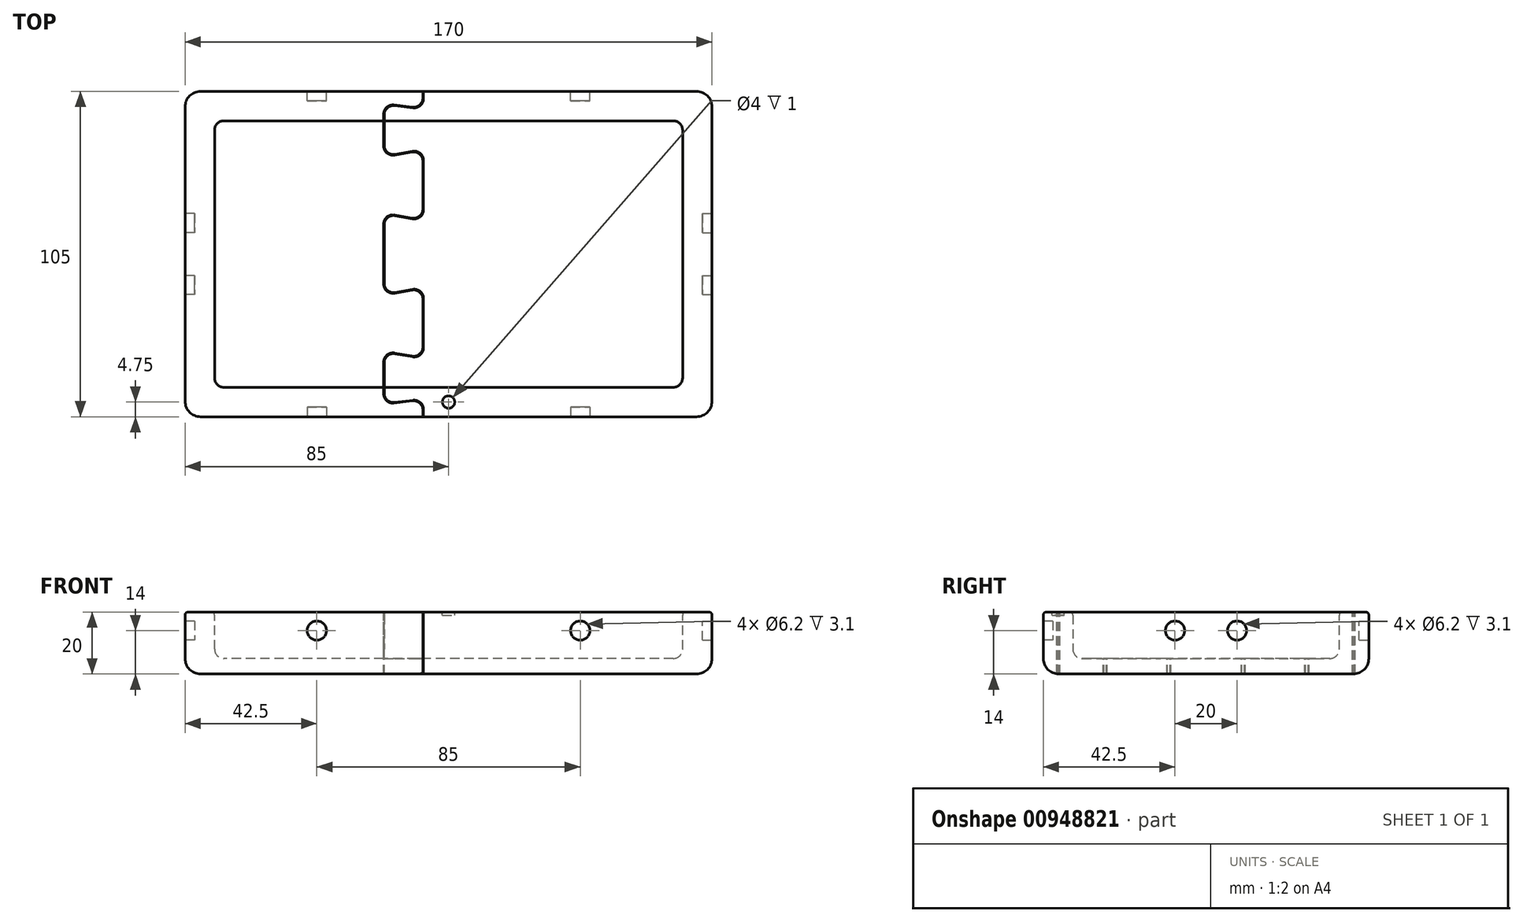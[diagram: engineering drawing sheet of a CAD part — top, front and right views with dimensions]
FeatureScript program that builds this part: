
annotation { "Feature Type Name" : "Feature", "Feature Type Description" : "" }
export const myFeature = defineFeature(function(context is Context, id is Id, definition is map)
    precondition{}
    {
        {
            var Q0;
            Q0=qCreatedBy(makeId("Top.planeOp"),FACE);
            var sketch = newSketch(context, id + "F0", { "sketchPlane" : qUnion([Q0])});
            skLineSegment(sketch, "E0.bottom", {"start": v(-85, 52.5) * mm, "end": v(85, 52.5) * mm});
            skLineSegment(sketch, "E0.top", {"start": v(-85, -52.5) * mm, "end": v(85, -52.5) * mm});
            skLineSegment(sketch, "E0.left", {"start": v(-85, 52.5) * mm, "end": v(-85, -52.5) * mm});
            skLineSegment(sketch, "E0.right", {"start": v(85, 52.5) * mm, "end": v(85, -52.5) * mm});
            skLineSegment(sketch, "E1.bottom", {"start": v(-72.5, 43) * mm, "end": v(72.5, 43) * mm});
            skLineSegment(sketch, "E1.top", {"start": v(-72.5, -43) * mm, "end": v(72.5, -43) * mm});
            skLineSegment(sketch, "E1.left", {"start": v(-75.5, 40) * mm, "end": v(-75.5, -40) * mm});
            skLineSegment(sketch, "E1.right", {"start": v(75.5, 40) * mm, "end": v(75.5, -40) * mm});
            skLineSegment(sketch, "E2.direction1", {"start": v(-75.5, -43) * mm, "end": v(15.26, -43) * mm, "construction": true});
            skPoint(sketch, "E3.visualSharp", {"position": v(-75.5, 43) * mm});
            skArc(sketch, "E3.filletArc", {"start": v(-72.5, 43) * mm, "mid": v(-74.62, 42.12) * mm, "end": v(-75.5, 40) * mm});
            skPoint(sketch, "E4.visualSharp", {"position": v(75.5, 43) * mm});
            skArc(sketch, "E4.filletArc", {"start": v(75.5, 40) * mm, "mid": v(74.62, 42.12) * mm, "end": v(72.5, 43) * mm});
            skPoint(sketch, "E5.visualSharp", {"position": v(75.5, -43) * mm});
            skArc(sketch, "E5.filletArc", {"start": v(72.5, -43) * mm, "mid": v(74.62, -42.12) * mm, "end": v(75.5, -40) * mm});
            skPoint(sketch, "E6.visualSharp", {"position": v(-75.5, -43) * mm});
            skArc(sketch, "E6.filletArc", {"start": v(-75.5, -40) * mm, "mid": v(-74.62, -42.12) * mm, "end": v(-72.5, -43) * mm});
            skLineSegment(sketch, "E7.direction1", {"start": v(-75.5, -43) * mm, "end": v(17, -43) * mm, "construction": true});
            skLineSegment(sketch, "E8", {"start": v(-85, 0) * mm, "end": v(85, 0) * mm, "construction": true});
            skLineSegment(sketch, "E9", {"start": v(0, -52.5) * mm, "end": v(0, 52.5) * mm, "construction": true});
            skCircle(sketch, "E10", {"center": v(0, -47.75) * mm, "radius": 2 * mm});
            skSolve(sketch);
        }
        {
            var Q0;
            Q0=makeQuery(id+"F0.imprint","IMPRINT",FACE,{"disambiguationData":[TD([[makeQuery(id+"F0.imprint","IMPRINT",EDGE,{"derivedFrom":sQuery(id+"F0.wireOp",EDGE,"E1.bottom")}),-1.0]])]});
            var Q1;
            Q1=makeQuery(id+"F0.imprint","IMPRINT",FACE,{"disambiguationData":[TD([[makeQuery(id+"F0.imprint","IMPRINT",EDGE,{"derivedFrom":sQuery(id+"F0.wireOp",EDGE,"E0.bottom")}),-1.0]])]});
            var Q2;
            Q2=makeQuery(id+"F0.imprint","IMPRINT",FACE,{"disambiguationData":[TD([[makeQuery(id+"F0.imprint","IMPRINT",EDGE,{"derivedFrom":sQuery(id+"F0.wireOp",EDGE,"E2.0.2.0")}),1.0]])]});
            var Q3;
            Q3=makeQuery(id+"F0.imprint","IMPRINT",FACE,{"disambiguationData":[TD([[makeQuery(id+"F0.imprint","IMPRINT",EDGE,{"derivedFrom":sQuery(id+"F0.wireOp",EDGE,"E2.0.3.0")}),1.0]])]});
            var Q4;
            Q4=makeQuery(id+"F0.imprint","IMPRINT",FACE,{"disambiguationData":[TD([[makeQuery(id+"F0.imprint","IMPRINT",EDGE,{"derivedFrom":sQuery(id+"F0.wireOp",EDGE,"E2.0.1.0")}),1.0]])]});
            var Q5;
            Q5=makeQuery(id+"F0.imprint","IMPRINT",FACE,{"disambiguationData":[TD([[makeQuery(id+"F0.imprint","IMPRINT",EDGE,{"derivedFrom":sQuery(id+"F0.wireOp",EDGE,"E7.0.1.2")}),1.0]])]});
            var Q6;
            Q6=makeQuery(id+"F0.imprint","IMPRINT",FACE,{"disambiguationData":[TD([[makeQuery(id+"F0.imprint","IMPRINT",EDGE,{"derivedFrom":sQuery(id+"F0.wireOp",EDGE,"E7.0.2.2")}),1.0]])]});
            var Q7;
            Q7=makeQuery(id+"F0.imprint","IMPRINT",FACE,{"disambiguationData":[TD([[makeQuery(id+"F0.imprint","IMPRINT",EDGE,{"derivedFrom":sQuery(id+"F0.wireOp",EDGE,"E7.0.3.2")}),1.0]])]});
            var Q8;
            Q8=makeQuery(id+"F0.imprint","IMPRINT",FACE,{"disambiguationData":[TD([[makeQuery(id+"F0.imprint","IMPRINT",EDGE,{"derivedFrom":sQuery(id+"F0.wireOp",EDGE,"E10")}),1.0]])]});
            extrude(context, id + "F1", {"entities" : qUnion([Q0, Q1, Q2, Q3, Q4, Q5, Q6, Q7, Q8]), "depth" : 20 * mm, "offsetDistance" : 25 * mm});
        }
        {
            var Q0;
            Q0=makeQuery(id+"F0.imprint","IMPRINT",FACE,{"disambiguationData":[TD([[makeQuery(id+"F0.imprint","IMPRINT",EDGE,{"derivedFrom":sQuery(id+"F0.wireOp",EDGE,"E1.bottom")}),-1.0]])]});
            var Q1;
            Q1=makeQuery(id+"F0.imprint","IMPRINT",FACE,{"disambiguationData":[TD([[makeQuery(id+"F0.imprint","IMPRINT",EDGE,{"derivedFrom":sQuery(id+"F0.wireOp",EDGE,"E2.0.1.0")}),1.0]])]});
            var Q2;
            Q2=makeQuery(id+"F0.imprint","IMPRINT",FACE,{"disambiguationData":[TD([[makeQuery(id+"F0.imprint","IMPRINT",EDGE,{"derivedFrom":sQuery(id+"F0.wireOp",EDGE,"E2.0.2.0")}),1.0]])]});
            var Q3;
            Q3=makeQuery(id+"F0.imprint","IMPRINT",FACE,{"disambiguationData":[TD([[makeQuery(id+"F0.imprint","IMPRINT",EDGE,{"derivedFrom":sQuery(id+"F0.wireOp",EDGE,"E2.0.3.0")}),1.0]])]});
            var Q4;
            Q4=makeQuery(id+"F0.imprint","IMPRINT",FACE,{"disambiguationData":[TD([[makeQuery(id+"F0.imprint","IMPRINT",EDGE,{"derivedFrom":sQuery(id+"F0.wireOp",EDGE,"E7.0.1.2")}),1.0]])]});
            var Q5;
            Q5=makeQuery(id+"F0.imprint","IMPRINT",FACE,{"disambiguationData":[TD([[makeQuery(id+"F0.imprint","IMPRINT",EDGE,{"derivedFrom":sQuery(id+"F0.wireOp",EDGE,"E7.0.2.2")}),1.0]])]});
            var Q6;
            Q6=makeQuery(id+"F0.imprint","IMPRINT",FACE,{"disambiguationData":[TD([[makeQuery(id+"F0.imprint","IMPRINT",EDGE,{"derivedFrom":sQuery(id+"F0.wireOp",EDGE,"E7.0.3.2")}),1.0]])]});
            extrude(context, id + "F2", {"entities" : qUnion([Q0, Q1, Q2, Q3, Q4, Q5, Q6]), "operationType" : NewBodyOperationType.REMOVE, "depth" : 15 * mm, "offsetDistance" : 25 * mm});
        }
        {
            var Q0;
            Q0=makeQuery(id+"F1.opExtrude","CAP_FACE",FACE,{"disambiguationData":[OSD([sQuery(id+"F0.wireOp",EDGE,"E0.bottom"),sQuery(id+"F0.wireOp",EDGE,"E0.top"),sQuery(id+"F0.wireOp",EDGE,"E0.left"),sQuery(id+"F0.wireOp",EDGE,"E0.right")])],"isStart":false});
            var Q1;
            Q1=makeQuery(id+"F1.opExtrude","SWEPT_EDGE",EDGE,{"disambiguationData":[OSD([sQuery(id+"F0.wireOp",EDGE,"E0.bottom"),sQuery(id+"F0.wireOp",EDGE,"E0.right")])]});
            var Q2;
            Q2=makeQuery(id+"F1.opExtrude","SWEPT_EDGE",EDGE,{"disambiguationData":[OSD([sQuery(id+"F0.wireOp",EDGE,"E0.bottom"),sQuery(id+"F0.wireOp",EDGE,"E0.left")])]});
            var Q3;
            Q3=makeQuery(id+"F1.opExtrude","SWEPT_EDGE",EDGE,{"disambiguationData":[OSD([sQuery(id+"F0.wireOp",EDGE,"E0.top"),sQuery(id+"F0.wireOp",EDGE,"E0.left")])]});
            var Q4;
            Q4=makeQuery(id+"F1.opExtrude","SWEPT_EDGE",EDGE,{"disambiguationData":[OSD([sQuery(id+"F0.wireOp",EDGE,"E0.top"),sQuery(id+"F0.wireOp",EDGE,"E0.right")])]});
            fillet(context, id + "F3", {"entities" : qUnion([Q0, Q1, Q2, Q3, Q4]), "radius" : 5 * mm, "tangentPropagation" : true, "allowEdgeOverflow" : false});
        }
        {
            var Q0;
            Q0=makeQuery(id+"F2.boolean.opBoolean","COPY",FACE,{"derivedFrom":makeQuery(id+"F2.opExtrude","CAP_FACE",FACE,{"disambiguationData":[OSD([sQuery(id+"F0.wireOp",EDGE,"E1.bottom"),sQuery(id+"F0.wireOp",EDGE,"E1.top"),sQuery(id+"F0.wireOp",EDGE,"E1.left"),sQuery(id+"F0.wireOp",EDGE,"E1.right"),sQuery(id+"F0.wireOp",EDGE,"E3.filletArc"),sQuery(id+"F0.wireOp",EDGE,"E4.filletArc"),sQuery(id+"F0.wireOp",EDGE,"E5.filletArc"),sQuery(id+"F0.wireOp",EDGE,"E6.filletArc")])],"isStart":false})});
            var Q1;
            Q1=makeQuery(id+"F2.boolean.opBoolean","COPY",FACE,{"derivedFrom":makeQuery(id+"F2.opExtrude","CAP_FACE",FACE,{"disambiguationData":[OSD([sQuery(id+"F0.wireOp",EDGE,"E7.0.1.2"),sQuery(id+"F0.wireOp",EDGE,"E7.0.1.4"),sQuery(id+"F0.wireOp",EDGE,"E7.0.1.5"),sQuery(id+"F0.wireOp",EDGE,"E7.0.1.6"),sQuery(id+"F0.wireOp",EDGE,"E7.0.1.7"),sQuery(id+"F0.wireOp",EDGE,"E7.0.1.9"),sQuery(id+"F0.wireOp",EDGE,"E7.0.1.11"),sQuery(id+"F0.wireOp",EDGE,"E7.0.1.12")])],"isStart":false})});
            var Q2;
            Q2=makeQuery(id+"F2.boolean.opBoolean","COPY",FACE,{"derivedFrom":makeQuery(id+"F2.opExtrude","CAP_FACE",FACE,{"disambiguationData":[OSD([sQuery(id+"F0.wireOp",EDGE,"E7.0.2.2"),sQuery(id+"F0.wireOp",EDGE,"E7.0.2.4"),sQuery(id+"F0.wireOp",EDGE,"E7.0.2.5"),sQuery(id+"F0.wireOp",EDGE,"E7.0.2.6"),sQuery(id+"F0.wireOp",EDGE,"E7.0.2.7"),sQuery(id+"F0.wireOp",EDGE,"E7.0.2.9"),sQuery(id+"F0.wireOp",EDGE,"E7.0.2.11"),sQuery(id+"F0.wireOp",EDGE,"E7.0.2.12")])],"isStart":false})});
            var Q3;
            Q3=makeQuery(id+"F2.boolean.opBoolean","COPY",FACE,{"derivedFrom":makeQuery(id+"F2.opExtrude","CAP_FACE",FACE,{"disambiguationData":[OSD([sQuery(id+"F0.wireOp",EDGE,"E7.0.3.2"),sQuery(id+"F0.wireOp",EDGE,"E7.0.3.4"),sQuery(id+"F0.wireOp",EDGE,"E7.0.3.5"),sQuery(id+"F0.wireOp",EDGE,"E7.0.3.6"),sQuery(id+"F0.wireOp",EDGE,"E7.0.3.7"),sQuery(id+"F0.wireOp",EDGE,"E7.0.3.9"),sQuery(id+"F0.wireOp",EDGE,"E7.0.3.11"),sQuery(id+"F0.wireOp",EDGE,"E7.0.3.12")])],"isStart":false})});
            fillet(context, id + "F4", {"entities" : qUnion([Q0, Q1, Q2, Q3]), "radius" : 3 * mm, "tangentPropagation" : true, "allowEdgeOverflow" : false});
        }
        {
            var Q0;
            Q0=makeQuery(id+"F1.opExtrude","CAP_FACE",FACE,{"disambiguationData":[OSD([sQuery(id+"F0.wireOp",EDGE,"E0.bottom"),sQuery(id+"F0.wireOp",EDGE,"E0.top"),sQuery(id+"F0.wireOp",EDGE,"E0.left"),sQuery(id+"F0.wireOp",EDGE,"E0.right")])],"isStart":true});
            fillet(context, id + "F5", {"entities" : qUnion([Q0]), "radius" : 1 * mm, "tangentPropagation" : true, "allowEdgeOverflow" : false});
        }
        {
            var Q0;
            Q0=makeQuery(id+"F1.opExtrude","SWEPT_FACE",FACE,{"disambiguationData":[OSD([sQuery(id+"F0.wireOp",EDGE,"E0.top")])]});
            var sketch = newSketch(context, id + "F6", { "sketchPlane" : qUnion([Q0])});
            skCircle(sketch, "E11", {"center": v(42.5, 6) * mm, "radius": 3.1 * mm});
            skCircle(sketch, "E12", {"center": v(-42.5, 6) * mm, "radius": 3.1 * mm});
            skSolve(sketch);
        }
        {
            var Q0;
            Q0=makeQuery(id+"F6.imprint","IMPRINT",FACE,{"disambiguationData":[TD([[makeQuery(id+"F6.imprint","IMPRINT",EDGE,{"derivedFrom":sQuery(id+"F6.wireOp",EDGE,"E11")}),1.0]])]});
            var Q1;
            Q1=makeQuery(id+"F6.imprint","IMPRINT",FACE,{"disambiguationData":[TD([[makeQuery(id+"F6.imprint","IMPRINT",EDGE,{"derivedFrom":sQuery(id+"F6.wireOp",EDGE,"E12")}),1.0]])]});
            extrude(context, id + "F7", {"entities" : qUnion([Q0, Q1]), "operationType" : NewBodyOperationType.REMOVE, "oppositeDirection" : true, "depth" : 3.1 * mm, "offsetDistance" : 25 * mm});
        }
        {
            var Q0;
            Q0=makeQuery(id+"F1.opExtrude","SWEPT_FACE",FACE,{"disambiguationData":[OSD([sQuery(id+"F0.wireOp",EDGE,"E0.bottom")])]});
            var sketch = newSketch(context, id + "F8", { "sketchPlane" : qUnion([Q0])});
            skCircle(sketch, "E13", {"center": v(42.5, 6) * mm, "radius": 3.1 * mm});
            skCircle(sketch, "E14", {"center": v(-42.5, 6) * mm, "radius": 3.1 * mm});
            skSolve(sketch);
        }
        {
            var Q0;
            Q0=makeQuery(id+"F8.imprint","IMPRINT",FACE,{"disambiguationData":[TD([[makeQuery(id+"F8.imprint","IMPRINT",EDGE,{"derivedFrom":sQuery(id+"F8.wireOp",EDGE,"E13")}),1.0]])]});
            var Q1;
            Q1=makeQuery(id+"F8.imprint","IMPRINT",FACE,{"disambiguationData":[TD([[makeQuery(id+"F8.imprint","IMPRINT",EDGE,{"derivedFrom":sQuery(id+"F8.wireOp",EDGE,"E14")}),1.0]])]});
            extrude(context, id + "F9", {"entities" : qUnion([Q0, Q1]), "operationType" : NewBodyOperationType.REMOVE, "oppositeDirection" : true, "depth" : 3.1 * mm, "offsetDistance" : 25 * mm});
        }
        {
            var Q0;
            Q0=makeQuery(id+"F1.opExtrude","SWEPT_FACE",FACE,{"disambiguationData":[OSD([sQuery(id+"F0.wireOp",EDGE,"E0.left")])]});
            var sketch = newSketch(context, id + "F10", { "sketchPlane" : qUnion([Q0])});
            skCircle(sketch, "E15", {"center": v(10, 6) * mm, "radius": 3.1 * mm});
            skCircle(sketch, "E16", {"center": v(-10, 6) * mm, "radius": 3.1 * mm});
            skSolve(sketch);
        }
        {
            var Q0;
            Q0=makeQuery(id+"F10.imprint","IMPRINT",FACE,{"disambiguationData":[TD([[makeQuery(id+"F10.imprint","IMPRINT",EDGE,{"derivedFrom":sQuery(id+"F10.wireOp",EDGE,"E15")}),1.0]])]});
            var Q1;
            Q1=makeQuery(id+"F10.imprint","IMPRINT",FACE,{"disambiguationData":[TD([[makeQuery(id+"F10.imprint","IMPRINT",EDGE,{"derivedFrom":sQuery(id+"F10.wireOp",EDGE,"E16")}),1.0]])]});
            extrude(context, id + "F11", {"entities" : qUnion([Q0, Q1]), "operationType" : NewBodyOperationType.REMOVE, "oppositeDirection" : true, "depth" : 3.1 * mm, "offsetDistance" : 25 * mm});
        }
        {
            var Q0;
            Q0=makeQuery(id+"F1.opExtrude","SWEPT_FACE",FACE,{"disambiguationData":[OSD([sQuery(id+"F0.wireOp",EDGE,"E0.right")])]});
            var sketch = newSketch(context, id + "F12", { "sketchPlane" : qUnion([Q0])});
            skCircle(sketch, "E17", {"center": v(10, 6) * mm, "radius": 3.1 * mm});
            skCircle(sketch, "E18", {"center": v(-10, 6) * mm, "radius": 3.1 * mm});
            skSolve(sketch);
        }
        {
            var Q0;
            Q0=makeQuery(id+"F12.imprint","IMPRINT",FACE,{"disambiguationData":[TD([[makeQuery(id+"F12.imprint","IMPRINT",EDGE,{"derivedFrom":sQuery(id+"F12.wireOp",EDGE,"E17")}),1.0]])]});
            var Q1;
            Q1=makeQuery(id+"F12.imprint","IMPRINT",FACE,{"disambiguationData":[TD([[makeQuery(id+"F12.imprint","IMPRINT",EDGE,{"derivedFrom":sQuery(id+"F12.wireOp",EDGE,"E18")}),1.0]])]});
            extrude(context, id + "F13", {"entities" : qUnion([Q0, Q1]), "operationType" : NewBodyOperationType.REMOVE, "oppositeDirection" : true, "depth" : 3.1 * mm, "offsetDistance" : 25 * mm});
        }
        {
            var Q0;
            Q0=makeQuery(id+"F0.imprint","IMPRINT",FACE,{"disambiguationData":[TD([[makeQuery(id+"F0.imprint","IMPRINT",EDGE,{"derivedFrom":sQuery(id+"F0.wireOp",EDGE,"E10")}),1.0]])]});
            var Q1;
            Q1=sQuery(id+"F0.wireOp",EDGE,"E10");
            extrude(context, id + "F14", {"entities" : qUnion([Q0]), "operationType" : NewBodyOperationType.REMOVE, "surfaceEntities" : qUnion([Q1]), "depth" : 1 * mm, "offsetDistance" : 25 * mm});
        }
        {
            var Q0;
            Q0=makeQuery(id+"F1.opExtrude","SWEPT_BODY",BODY,{"disambiguationData":[OSD([sQuery(id+"F0.wireOp",EDGE,"E0.bottom"),sQuery(id+"F0.wireOp",EDGE,"E0.top"),sQuery(id+"F0.wireOp",EDGE,"E0.left"),sQuery(id+"F0.wireOp",EDGE,"E0.right")])]});
            var Q1;
            Q1=sQuery(id+"F0.wireOp",EDGE,"E9");
            transform(context, id + "F15", {"entities" : qUnion([Q0]), "transformType" : TransformType.ROTATION, "transformAxis" : qUnion([Q1]), "angle" : 180 * degree, "makeCopy" : false});
        }
        {
            var Q0;
            Q0=qCreatedBy(makeId("Top.planeOp"),FACE);
            var sketch = newSketch(context, id + "F16", { "sketchPlane" : qUnion([Q0])});
            skLineSegment(sketch, "E19", {"start": v(-20.96, 0) * mm, "end": v(-20.96, 9.66) * mm});
            skLineSegment(sketch, "E20", {"start": v(-17.44, 12.62) * mm, "end": v(-11.8, 11.62) * mm});
            skLineSegment(sketch, "E21", {"start": v(-8.28, 14.58) * mm, "end": v(-8.28, 29.97) * mm});
            skLineSegment(sketch, "E22", {"start": v(-11.8, 32.93) * mm, "end": v(-17.44, 31.93) * mm});
            skLineSegment(sketch, "E23", {"start": v(-20.96, 34.89) * mm, "end": v(-20.96, 45.12) * mm});
            skLineSegment(sketch, "E24", {"start": v(-17.6, 48.1) * mm, "end": v(-11.63, 47.4) * mm});
            skLineSegment(sketch, "E25", {"start": v(-8.28, 50.38) * mm, "end": v(-8.28, 69.12) * mm});
            skLineSegment(sketch, "E26", {"start": v(-8.28, 69.12) * mm, "end": v(-109.53, 69.12) * mm});
            skLineSegment(sketch, "E27", {"start": v(-109.53, 69.12) * mm, "end": v(-109.53, 0) * mm});
            skLineSegment(sketch, "E28.MirrorCS", {"start": v(-20.96, 0) * mm, "end": v(-20.96, -9.66) * mm});
            skLineSegment(sketch, "E29.MirrorCS", {"start": v(-17.44, -12.62) * mm, "end": v(-11.8, -11.62) * mm});
            skLineSegment(sketch, "E30.MirrorCS", {"start": v(-8.28, -14.58) * mm, "end": v(-8.28, -29.97) * mm});
            skLineSegment(sketch, "E31.MirrorCS", {"start": v(-11.8, -32.93) * mm, "end": v(-17.44, -31.93) * mm});
            skLineSegment(sketch, "E32.MirrorCS", {"start": v(-20.96, -34.89) * mm, "end": v(-20.96, -45.12) * mm});
            skLineSegment(sketch, "E33.MirrorCS", {"start": v(-17.6, -48.1) * mm, "end": v(-11.63, -47.4) * mm});
            skLineSegment(sketch, "E34.MirrorCS", {"start": v(-8.28, -50.38) * mm, "end": v(-8.28, -69.12) * mm});
            skLineSegment(sketch, "E35.MirrorCS", {"start": v(-8.28, -69.12) * mm, "end": v(-109.53, -69.12) * mm});
            skLineSegment(sketch, "E36.MirrorCS", {"start": v(-109.53, -69.12) * mm, "end": v(-109.53, 0) * mm});
            skLineSegment(sketch, "E37", {"start": v(-8.08, 69.12) * mm, "end": v(105.82, 69.12) * mm});
            skLineSegment(sketch, "E38", {"start": v(105.82, 69.12) * mm, "end": v(105.82, -69.12) * mm});
            skLineSegment(sketch, "E39", {"start": v(105.82, -69.12) * mm, "end": v(-8.08, -69.12) * mm});
            skLineSegment(sketch, "E40.0", {"start": v(-8.08, 50.15) * mm, "end": v(-8.08, 69.12) * mm});
            skLineSegment(sketch, "E40.1", {"start": v(-17.4, 47.88) * mm, "end": v(-11.43, 47.17) * mm});
            skLineSegment(sketch, "E40.2", {"start": v(-20.76, 35.13) * mm, "end": v(-20.76, 44.9) * mm});
            skLineSegment(sketch, "E40.3", {"start": v(-20.76, 0) * mm, "end": v(-20.76, 9.42) * mm});
            skLineSegment(sketch, "E40.4", {"start": v(-17.24, 12.38) * mm, "end": v(-11.6, 11.38) * mm});
            skLineSegment(sketch, "E40.5", {"start": v(-8.08, 14.34) * mm, "end": v(-8.08, 30.21) * mm});
            skLineSegment(sketch, "E40.6", {"start": v(-11.6, 33.16) * mm, "end": v(-17.24, 32.17) * mm});
            skLineSegment(sketch, "E41.MirrorCS", {"start": v(-8.08, -50.15) * mm, "end": v(-8.08, -69.12) * mm});
            skLineSegment(sketch, "E42.MirrorCS", {"start": v(-17.4, -47.88) * mm, "end": v(-11.43, -47.17) * mm});
            skLineSegment(sketch, "E43.MirrorCS", {"start": v(-20.76, -35.13) * mm, "end": v(-20.76, -44.9) * mm});
            skLineSegment(sketch, "E44.MirrorCS", {"start": v(-11.6, -33.16) * mm, "end": v(-17.24, -32.17) * mm});
            skLineSegment(sketch, "E45.MirrorCS", {"start": v(-8.08, -14.34) * mm, "end": v(-8.08, -30.21) * mm});
            skLineSegment(sketch, "E46.MirrorCS", {"start": v(-20.76, 0) * mm, "end": v(-20.76, -9.42) * mm});
            skLineSegment(sketch, "E47.MirrorCS", {"start": v(-17.24, -12.38) * mm, "end": v(-11.6, -11.38) * mm});
            skPoint(sketch, "E48.visualSharp", {"position": v(-8.28, 47) * mm});
            skArc(sketch, "E48.filletArc", {"start": v(-11.63, 47.4) * mm, "mid": v(-9.29, 48.13) * mm, "end": v(-8.28, 50.38) * mm});
            skPoint(sketch, "E49.visualSharp", {"position": v(-8.08, 46.77) * mm});
            skArc(sketch, "E49.filletArc", {"start": v(-11.43, 47.17) * mm, "mid": v(-9.09, 47.9) * mm, "end": v(-8.08, 50.15) * mm});
            skPoint(sketch, "E50.visualSharp", {"position": v(-20.96, 48.5) * mm});
            skArc(sketch, "E50.filletArc", {"start": v(-17.6, 48.1) * mm, "mid": v(-19.95, 47.37) * mm, "end": v(-20.96, 45.12) * mm});
            skPoint(sketch, "E51.visualSharp", {"position": v(-20.76, 48.27) * mm});
            skArc(sketch, "E51.filletArc", {"start": v(-17.4, 47.88) * mm, "mid": v(-19.75, 47.14) * mm, "end": v(-20.76, 44.9) * mm});
            skPoint(sketch, "E52.visualSharp", {"position": v(-20.76, 31.55) * mm});
            skArc(sketch, "E52.filletArc", {"start": v(-20.76, 35.13) * mm, "mid": v(-19.68, 32.83) * mm, "end": v(-17.24, 32.17) * mm});
            skPoint(sketch, "E53.visualSharp", {"position": v(-20.96, 31.31) * mm});
            skArc(sketch, "E53.filletArc", {"start": v(-20.96, 34.89) * mm, "mid": v(-19.88, 32.59) * mm, "end": v(-17.44, 31.93) * mm});
            skPoint(sketch, "E54.visualSharp", {"position": v(-8.28, 33.55) * mm});
            skArc(sketch, "E54.filletArc", {"start": v(-8.28, 29.97) * mm, "mid": v(-9.35, 32.27) * mm, "end": v(-11.8, 32.93) * mm});
            skPoint(sketch, "E55.visualSharp", {"position": v(-8.08, 33.79) * mm});
            skArc(sketch, "E55.filletArc", {"start": v(-8.08, 30.21) * mm, "mid": v(-9.15, 32.5) * mm, "end": v(-11.6, 33.16) * mm});
            skPoint(sketch, "E56.visualSharp", {"position": v(-8.28, 11) * mm});
            skArc(sketch, "E56.filletArc", {"start": v(-11.8, 11.62) * mm, "mid": v(-9.35, 12.28) * mm, "end": v(-8.28, 14.58) * mm});
            skPoint(sketch, "E57.visualSharp", {"position": v(-8.08, 10.76) * mm});
            skArc(sketch, "E57.filletArc", {"start": v(-11.6, 11.38) * mm, "mid": v(-9.15, 12.04) * mm, "end": v(-8.08, 14.34) * mm});
            skPoint(sketch, "E58.visualSharp", {"position": v(-20.96, 13.24) * mm});
            skArc(sketch, "E58.filletArc", {"start": v(-17.44, 12.62) * mm, "mid": v(-19.88, 11.96) * mm, "end": v(-20.96, 9.66) * mm});
            skPoint(sketch, "E59.visualSharp", {"position": v(-20.76, 13) * mm});
            skArc(sketch, "E59.filletArc", {"start": v(-17.24, 12.38) * mm, "mid": v(-19.68, 11.72) * mm, "end": v(-20.76, 9.42) * mm});
            skPoint(sketch, "E60.visualSharp", {"position": v(-20.76, -13) * mm});
            skArc(sketch, "E60.filletArc", {"start": v(-20.76, -9.42) * mm, "mid": v(-19.68, -11.72) * mm, "end": v(-17.24, -12.38) * mm});
            skPoint(sketch, "E61.visualSharp", {"position": v(-20.96, -13.24) * mm});
            skArc(sketch, "E61.filletArc", {"start": v(-20.96, -9.66) * mm, "mid": v(-19.88, -11.96) * mm, "end": v(-17.44, -12.62) * mm});
            skPoint(sketch, "E62.visualSharp", {"position": v(-8.28, -11) * mm});
            skArc(sketch, "E62.filletArc", {"start": v(-8.28, -14.58) * mm, "mid": v(-9.35, -12.28) * mm, "end": v(-11.8, -11.62) * mm});
            skPoint(sketch, "E63.visualSharp", {"position": v(-8.08, -10.76) * mm});
            skArc(sketch, "E63.filletArc", {"start": v(-8.08, -14.34) * mm, "mid": v(-9.15, -12.04) * mm, "end": v(-11.6, -11.38) * mm});
            skPoint(sketch, "E64.visualSharp", {"position": v(-8.28, -33.55) * mm});
            skArc(sketch, "E64.filletArc", {"start": v(-11.8, -32.93) * mm, "mid": v(-9.35, -32.27) * mm, "end": v(-8.28, -29.97) * mm});
            skPoint(sketch, "E65.visualSharp", {"position": v(-8.08, -33.79) * mm});
            skArc(sketch, "E65.filletArc", {"start": v(-11.6, -33.16) * mm, "mid": v(-9.15, -32.5) * mm, "end": v(-8.08, -30.21) * mm});
            skPoint(sketch, "E66.visualSharp", {"position": v(-20.96, -31.31) * mm});
            skArc(sketch, "E66.filletArc", {"start": v(-17.44, -31.93) * mm, "mid": v(-19.88, -32.59) * mm, "end": v(-20.96, -34.89) * mm});
            skPoint(sketch, "E67.visualSharp", {"position": v(-20.76, -31.55) * mm});
            skArc(sketch, "E67.filletArc", {"start": v(-17.24, -32.17) * mm, "mid": v(-19.68, -32.83) * mm, "end": v(-20.76, -35.13) * mm});
            skPoint(sketch, "E68.visualSharp", {"position": v(-20.76, -48.27) * mm});
            skArc(sketch, "E68.filletArc", {"start": v(-20.76, -44.9) * mm, "mid": v(-19.75, -47.14) * mm, "end": v(-17.4, -47.88) * mm});
            skPoint(sketch, "E69.visualSharp", {"position": v(-20.96, -48.5) * mm});
            skArc(sketch, "E69.filletArc", {"start": v(-20.96, -45.12) * mm, "mid": v(-19.95, -47.37) * mm, "end": v(-17.6, -48.1) * mm});
            skPoint(sketch, "E70.visualSharp", {"position": v(-8.08, -46.77) * mm});
            skArc(sketch, "E70.filletArc", {"start": v(-8.08, -50.15) * mm, "mid": v(-9.09, -47.9) * mm, "end": v(-11.43, -47.17) * mm});
            skPoint(sketch, "E71.visualSharp", {"position": v(-8.28, -47) * mm});
            skArc(sketch, "E71.filletArc", {"start": v(-8.28, -50.38) * mm, "mid": v(-9.29, -48.13) * mm, "end": v(-11.63, -47.4) * mm});
            skSolve(sketch);
        }
        {
            var Q0;
            Q0=makeQuery(id+"F16.imprint","IMPRINT",FACE,{"disambiguationData":[TD([[makeQuery(id+"F16.imprint","IMPRINT",EDGE,{"derivedFrom":sQuery(id+"F16.wireOp",EDGE,"E19")}),1.0]])]});
            extrude(context, id + "F17", {"entities" : qUnion([Q0]), "oppositeDirection" : true, "depth" : 25 * mm, "offsetDistance" : 25 * mm});
        }
        {
            var Q0;
            Q0=makeQuery(id+"F16.imprint","IMPRINT",FACE,{"disambiguationData":[TD([[makeQuery(id+"F16.imprint","IMPRINT",EDGE,{"derivedFrom":sQuery(id+"F16.wireOp",EDGE,"E37")}),-1.0]])]});
            extrude(context, id + "F18", {"entities" : qUnion([Q0]), "oppositeDirection" : true, "depth" : 25 * mm, "offsetDistance" : 25 * mm});
        }
        {
            var Q0;
            Q0=makeQuery(id+"F1.opExtrude","SWEPT_BODY",BODY,{"disambiguationData":[OSD([sQuery(id+"F0.wireOp",EDGE,"E0.bottom"),sQuery(id+"F0.wireOp",EDGE,"E0.top"),sQuery(id+"F0.wireOp",EDGE,"E0.left"),sQuery(id+"F0.wireOp",EDGE,"E0.right")])]});
            transform(context, id + "F19", {"entities" : qUnion([Q0]), "transformType" : TransformType.TRANSLATION_3D, "dx" : 0 * mm, "dy" : 0 * mm, "dz" : 0 * mm, "makeCopy" : true});
        }
        {
            var Q0;
            Q0=makeQuery(id+"F1.opExtrude","SWEPT_BODY",BODY,{"disambiguationData":[OSD([sQuery(id+"F0.wireOp",EDGE,"E0.bottom"),sQuery(id+"F0.wireOp",EDGE,"E0.top"),sQuery(id+"F0.wireOp",EDGE,"E0.left"),sQuery(id+"F0.wireOp",EDGE,"E0.right")])]});
            var Q1;
            Q1=makeQuery(id+"F17.opExtrude","SWEPT_BODY",BODY,{"disambiguationData":[OSD([sQuery(id+"F16.wireOp",EDGE,"E19"),sQuery(id+"F16.wireOp",EDGE,"E20"),sQuery(id+"F16.wireOp",EDGE,"E21"),sQuery(id+"F16.wireOp",EDGE,"E22"),sQuery(id+"F16.wireOp",EDGE,"E23"),sQuery(id+"F16.wireOp",EDGE,"E24"),sQuery(id+"F16.wireOp",EDGE,"E25"),sQuery(id+"F16.wireOp",EDGE,"E26"),sQuery(id+"F16.wireOp",EDGE,"E27"),sQuery(id+"F16.wireOp",EDGE,"E28.MirrorCS"),sQuery(id+"F16.wireOp",EDGE,"E29.MirrorCS"),sQuery(id+"F16.wireOp",EDGE,"E30.MirrorCS"),sQuery(id+"F16.wireOp",EDGE,"E31.MirrorCS"),sQuery(id+"F16.wireOp",EDGE,"E32.MirrorCS"),sQuery(id+"F16.wireOp",EDGE,"E33.MirrorCS"),sQuery(id+"F16.wireOp",EDGE,"E34.MirrorCS"),sQuery(id+"F16.wireOp",EDGE,"E35.MirrorCS"),sQuery(id+"F16.wireOp",EDGE,"E36.MirrorCS")])]});
            booleanBodies(context, id + "F20", {"operationType" : BooleanOperationType.INTERSECTION, "tools" : qUnion([Q0, Q1])});
        }
        {
            var Q0;
            Q0=makeQuery(id+"F18.opExtrude","SWEPT_BODY",BODY,{"disambiguationData":[OSD([sQuery(id+"F16.wireOp",EDGE,"E37"),sQuery(id+"F16.wireOp",EDGE,"E38"),sQuery(id+"F16.wireOp",EDGE,"E39"),sQuery(id+"F16.wireOp",EDGE,"E40.0"),sQuery(id+"F16.wireOp",EDGE,"E40.1"),sQuery(id+"F16.wireOp",EDGE,"E40.2"),sQuery(id+"F16.wireOp",EDGE,"E40.3"),sQuery(id+"F16.wireOp",EDGE,"E40.4"),sQuery(id+"F16.wireOp",EDGE,"E40.5"),sQuery(id+"F16.wireOp",EDGE,"E40.6"),sQuery(id+"F16.wireOp",EDGE,"E41.MirrorCS"),sQuery(id+"F16.wireOp",EDGE,"E42.MirrorCS"),sQuery(id+"F16.wireOp",EDGE,"E43.MirrorCS"),sQuery(id+"F16.wireOp",EDGE,"E44.MirrorCS"),sQuery(id+"F16.wireOp",EDGE,"E45.MirrorCS"),sQuery(id+"F16.wireOp",EDGE,"E46.MirrorCS"),sQuery(id+"F16.wireOp",EDGE,"E47.MirrorCS"),sQuery(id+"F16.wireOp",EDGE,"E49.filletArc"),sQuery(id+"F16.wireOp",EDGE,"E51.filletArc"),sQuery(id+"F16.wireOp",EDGE,"E52.filletArc"),sQuery(id+"F16.wireOp",EDGE,"E55.filletArc"),sQuery(id+"F16.wireOp",EDGE,"E57.filletArc"),sQuery(id+"F16.wireOp",EDGE,"E59.filletArc"),sQuery(id+"F16.wireOp",EDGE,"E60.filletArc"),sQuery(id+"F16.wireOp",EDGE,"E63.filletArc"),sQuery(id+"F16.wireOp",EDGE,"E65.filletArc"),sQuery(id+"F16.wireOp",EDGE,"E67.filletArc"),sQuery(id+"F16.wireOp",EDGE,"E68.filletArc"),sQuery(id+"F16.wireOp",EDGE,"E70.filletArc")])]});
            var Q1;
            Q1=makeQuery(id+"F19.opPattern","COPY",BODY,{"derivedFrom":makeQuery(id+"F1.opExtrude","SWEPT_BODY",BODY,{"disambiguationData":[OSD([sQuery(id+"F0.wireOp",EDGE,"E0.bottom"),sQuery(id+"F0.wireOp",EDGE,"E0.top"),sQuery(id+"F0.wireOp",EDGE,"E0.left"),sQuery(id+"F0.wireOp",EDGE,"E0.right")])]}),"instanceName":"1"});
            booleanBodies(context, id + "F21", {"operationType" : BooleanOperationType.INTERSECTION, "tools" : qUnion([Q0, Q1])});
        }
    });
